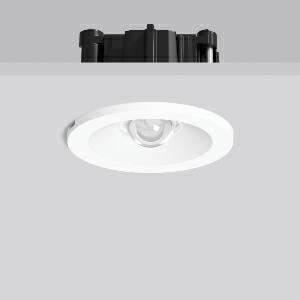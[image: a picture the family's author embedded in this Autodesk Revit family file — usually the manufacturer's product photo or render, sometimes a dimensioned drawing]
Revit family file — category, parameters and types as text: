
# Revit family: turia_l_672412_002_07_743a
name_source: partatom
category: Lighting Fixtures
units: mm (PartAtom-declared; Revit-internal decimal feet)

## family parameters
Cut with Voids When Loaded = No
Host = Face
Light Source = No
Part Type = Normal
Room Calculation Point = No
Round Connector Dimension = Use Diameter
Shared = No

## types (1)
- TURIA L (1 x LED Modul 765, 270 lm, 6500)
    Apparent Load = 5 VA
    CIE Flux Codes = 16 58 99 100 100
    Color Rendering = 70
    Color Temperature = 6500
    Default Elevation = 1800 mm
    Description = Series: TURIA L
Round emergency luminaire for escape route lighting. Housing: die-cast aluminium. Bezel ring: plastic. With plastic lenses for area lighting. Self-contained system with automatic self-test and feedback via DALI bus, only to RZB DALI monitoring system. With enclosed separate ceiling mounting ring also suitable for ceiling cut-outs of Ø 68 mm. 
Colour: white
Diameter: 62 mm
Height: 3 mm
Cut-out diameter: 54-68 mm
Recess height: 76-162 mm
Luminaire: recess height: 42 mm
Weight: 430 g
Operating mode: non-maintained power mode
Duration time: 3 h
Lamp: LED
Socket: without socket
Colour temperature: 6500K
Colour rendering index (CRI): 70
System power: 5.3 W
Rated luminous flux: 270 lm
Luminous flux, emergency: 190 lm
System power, emergency: -
Control gear: Regulated power supply
Protection class: II
Type of protection: IP 20
    Height = 0 mm  [stored 0 ft]
    Lamp = 1 x LED Modul 765
    Lamp Light Flux = 270 lm
    Lamp count = 1
    Length = 62 mm  [stored 0.203412 ft]
    Lifetime = 50000 h
    Luminous efficacy = 51 lm/W
    Manufacturer = RZB
    ModVariant = No
    Model = 672412.002.07
    Mounting Place = Ceiling
    Mounting Type = Recessed
    Number of Poles = 1
    OnlyDefault = Yes
    Power Factor = 1
    Product Name = TURIA L
    Product group = Recessed ceiling luminaires
    ProductGroupID = 405
    Protection Class = Protection class II
    Protection Degree = IP 20
    RLX_Detail_Level = 1
    RLX_Emergency_Light_Flux = 190 lm
    RLX_Emergency_Type = 3
    RLX_Emergency_Type_DB = Yes
    RlxData = <blob elided: 35989 chars, md5=d015425b>
    Socket = socket
    Standby Power = 0 W
    System Light Flux = 270 lm
    System Power = 5 W
    Type Comments = Product without accessories
    Type Image = 672412.002.jpg
    URL = http://relux.com
    VarID = ---
    Voltage = 230 V
    Voltage Range = 220-240 V
    Weight = 0.00 kg
    Width = 0 mm  [stored 0 ft]

note: [stored X ft] marks values corroborated as IEEE doubles in the binary element streams (Revit-internal decimal feet)

## geometry (parser evidence)
native form markers: Blend x4, Sweep x10
no freeform markers — native parametric forms only
